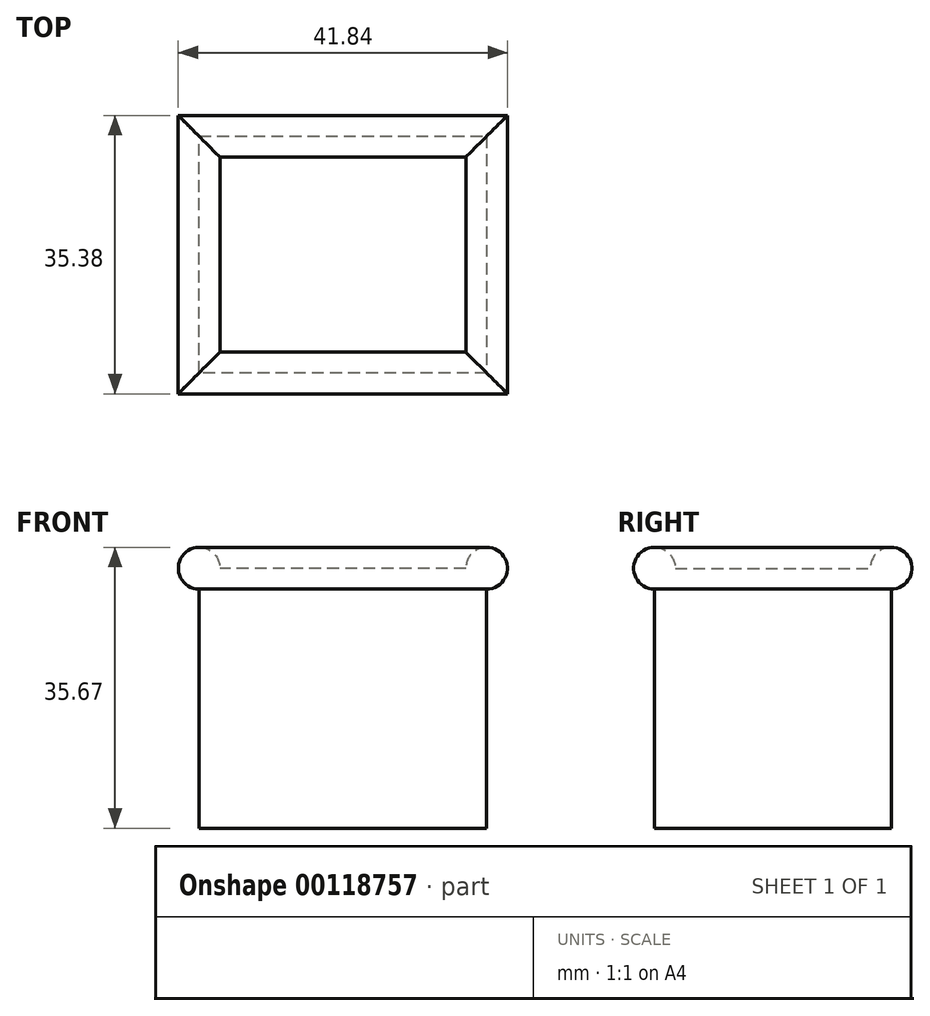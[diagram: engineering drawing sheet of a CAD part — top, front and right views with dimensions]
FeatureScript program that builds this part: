
annotation { "Feature Type Name" : "Feature", "Feature Type Description" : "" }
export const myFeature = defineFeature(function(context is Context, id is Id, definition is map)
    precondition{}
    {
        {
            var Q0;
            Q0=qCreatedBy(makeId("Top.planeOp"),FACE);
            var sketch = newSketch(context, id + "F0", { "sketchPlane" : qUnion([Q0])});
            skLineSegment(sketch, "E0.bottom", {"start": v(0, 0) * mm, "end": v(36.54, 0) * mm});
            skLineSegment(sketch, "E0.top", {"start": v(0, 30.08) * mm, "end": v(36.54, 30.08) * mm});
            skLineSegment(sketch, "E0.left", {"start": v(0, 0) * mm, "end": v(0, 30.08) * mm});
            skLineSegment(sketch, "E0.right", {"start": v(36.54, 0) * mm, "end": v(36.54, 30.08) * mm});
            skSolve(sketch);
        }
        {
            var Q0;
            Q0 = qSketchRegion(id + "F0", true);
            var Q1;
            Q1 = qConstructionFilter(qBodyType(qCreatedBy(id + "F0" ,EDGE), BodyType.WIRE), ConstructionObject.NO);
            extrude(context, id + "F1", {"entities" : qUnion([Q0]), "surfaceEntities" : qUnion([Q1]), "depth" : 33.02 * mm});
        }
        {
            var Q0;
            Q0=makeQuery(id+"F1.opExtrude","SWEPT_FACE",FACE,{"disambiguationData":[OSD([sQuery(id+"F0.wireOp",EDGE,"E0.right")])]});
            var sketch = newSketch(context, id + "F2", { "sketchPlane" : qUnion([Q0])});
            skArc(sketch, "E1", {"start": v(2.65, 33.02) * mm, "mid": v(-1.87, 34.9) * mm, "end": v(0, 30.37) * mm});
            skLineSegment(sketch, "E2", {"start": v(0, 33.02) * mm, "end": v(2.65, 33.02) * mm});
            skLineSegment(sketch, "E3", {"start": v(0, 33.02) * mm, "end": v(0, 30.37) * mm});
            skSolve(sketch);
        }
        {
            var Q0;
            Q0 = qSketchRegion(id + "F2", true);
            var Q1;
            Q1=makeQuery(id+"F1.opExtrude","CAP_EDGE",EDGE,{"disambiguationData":[OSD([sQuery(id+"F0.wireOp",EDGE,"E0.bottom")])],"isStart":false});
            var Q2;
            Q2=makeQuery(id+"F1.opExtrude","CAP_EDGE",EDGE,{"disambiguationData":[OSD([sQuery(id+"F0.wireOp",EDGE,"E0.right")])],"isStart":false});
            var Q3;
            Q3=makeQuery(id+"F1.opExtrude","CAP_EDGE",EDGE,{"disambiguationData":[OSD([sQuery(id+"F0.wireOp",EDGE,"E0.left")])],"isStart":false});
            var Q4;
            Q4=makeQuery(id+"F1.opExtrude","CAP_EDGE",EDGE,{"disambiguationData":[OSD([sQuery(id+"F0.wireOp",EDGE,"E0.top")])],"isStart":false});
            sweep(context, id + "F3", {"operationType" : NewBodyOperationType.ADD, "profiles" : qUnion([Q0]), "path" : qUnion([Q1, Q2, Q3, Q4])});
        }
    });
